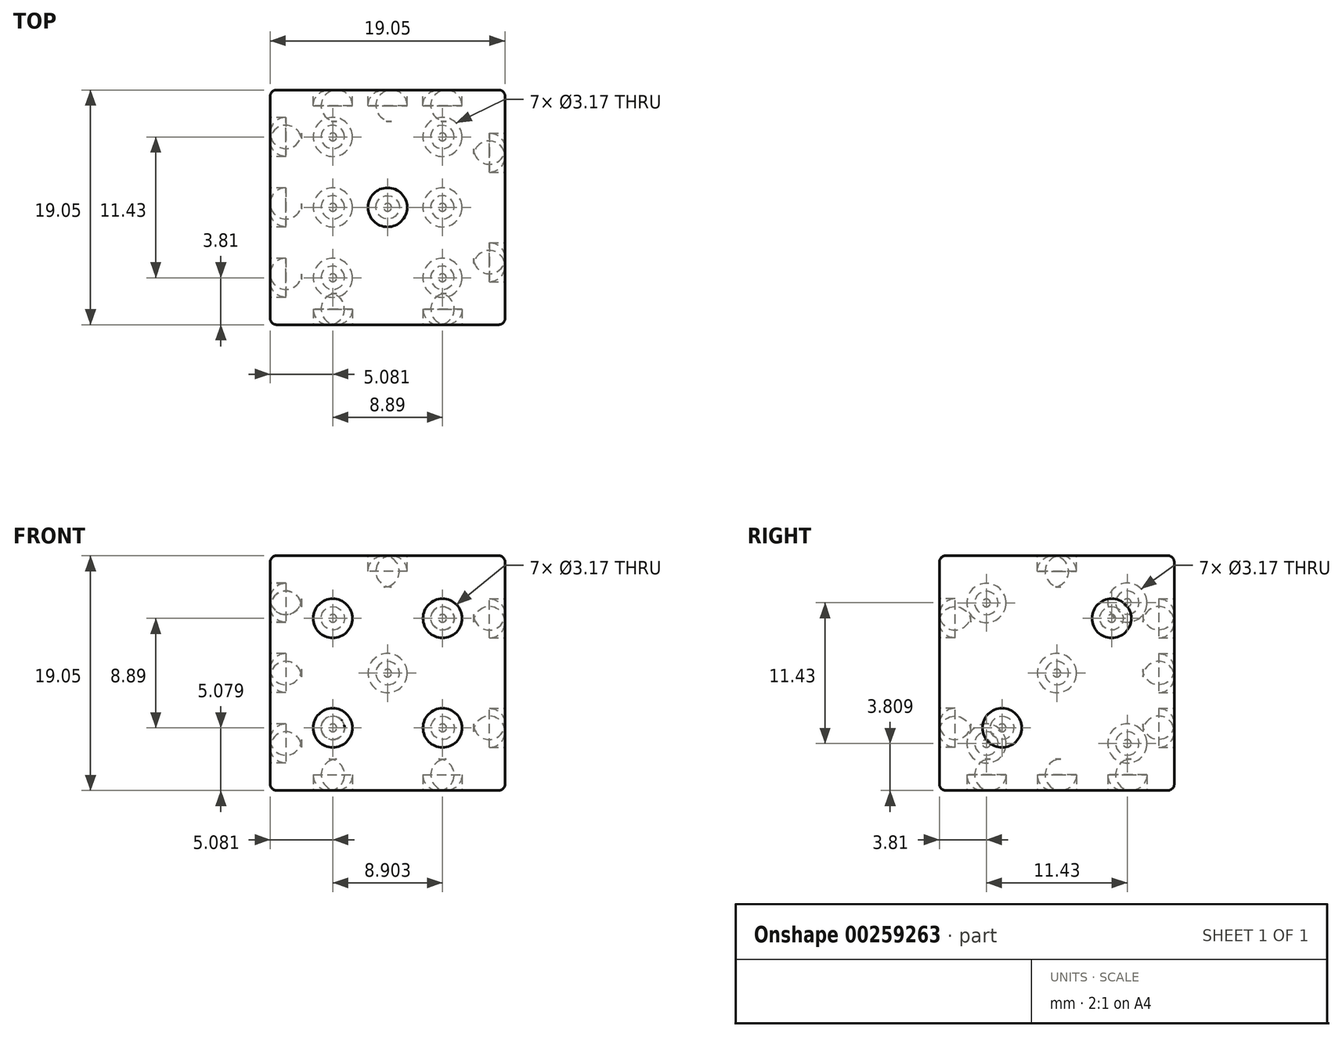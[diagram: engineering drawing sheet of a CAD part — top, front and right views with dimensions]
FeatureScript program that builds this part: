
annotation { "Feature Type Name" : "Feature", "Feature Type Description" : "" }
export const myFeature = defineFeature(function(context is Context, id is Id, definition is map)
    precondition{}
    {
        {
            var Q0;
            Q0=qCreatedBy(makeId("Front.planeOp"),FACE);
            var sketch = newSketch(context, id + "F0", { "sketchPlane" : qUnion([Q0])});
            skLineSegment(sketch, "E0.bottom", {"start": v(0, 0) * mm, "end": v(19.05, 0) * mm});
            skLineSegment(sketch, "E0.top", {"start": v(0, 19.05) * mm, "end": v(19.05, 19.05) * mm});
            skLineSegment(sketch, "E0.left", {"start": v(0, 0) * mm, "end": v(0, 19.05) * mm});
            skLineSegment(sketch, "E0.right", {"start": v(19.05, 0) * mm, "end": v(19.05, 19.05) * mm});
            skSolve(sketch);
        }
        {
            var Q0;
            Q0=makeQuery(id+"F0.imprint","IMPRINT",FACE,{"disambiguationData":[TD([[makeQuery(id+"F0.imprint","IMPRINT",EDGE,{"derivedFrom":sQuery(id+"F0.wireOp",EDGE,"E0.bottom")}),1.0]])]});
            extrude(context, id + "F1", {"entities" : qUnion([Q0]), "depth" : 19.05 * mm});
        }
        {
            var Q0;
            Q0=makeQuery(id+"F1.opExtrude","SWEPT_FACE",FACE,{"disambiguationData":[OSD([sQuery(id+"F0.wireOp",EDGE,"E0.top")])]});
            var sketch = newSketch(context, id + "F2", { "sketchPlane" : qUnion([Q0])});
            skCircle(sketch, "E1", {"center": v(9.52, -9.53) * mm, "radius": 1.59 * mm});
            skPoint(sketch, "E1.centerSnap0", {"position": v(9.52, 0) * mm});
            skPoint(sketch, "E1.centerSnap1", {"position": v(0, -9.53) * mm});
            skSolve(sketch);
        }
        {
            var Q0;
            Q0=makeQuery(id+"F2.imprint","IMPRINT",FACE,{"disambiguationData":[TD([[makeQuery(id+"F2.imprint","IMPRINT",EDGE,{"derivedFrom":sQuery(id+"F2.wireOp",EDGE,"E1")}),1.0]])]});
            extrude(context, id + "F3", {"entities" : qUnion([Q0]), "operationType" : NewBodyOperationType.REMOVE, "oppositeDirection" : true, "depth" : 2.54 * mm});
        }
        {
            var Q0;
            Q0=makeQuery(id+"F1.opExtrude","SWEPT_FACE",FACE,{"disambiguationData":[OSD([sQuery(id+"F0.wireOp",EDGE,"E0.bottom")])]});
            var sketch = newSketch(context, id + "F4", { "sketchPlane" : qUnion([Q0])});
            skCircle(sketch, "E2", {"center": v(5.08, 15.24) * mm, "radius": 1.59 * mm});
            skCircle(sketch, "E3", {"center": v(5.08, 9.53) * mm, "radius": 1.59 * mm});
            skCircle(sketch, "E4", {"center": v(5.08, 3.81) * mm, "radius": 1.59 * mm});
            skPoint(sketch, "E5", {"position": v(0, 9.53) * mm});
            skCircle(sketch, "E6", {"center": v(13.97, 15.24) * mm, "radius": 1.59 * mm});
            skCircle(sketch, "E7", {"center": v(13.97, 9.53) * mm, "radius": 1.59 * mm});
            skCircle(sketch, "E8", {"center": v(13.97, 3.81) * mm, "radius": 1.59 * mm});
            skSolve(sketch);
        }
        {
            var Q0;
            Q0=makeQuery(id+"F4.imprint","IMPRINT",FACE,{"disambiguationData":[TD([[makeQuery(id+"F4.imprint","IMPRINT",EDGE,{"derivedFrom":sQuery(id+"F4.wireOp",EDGE,"E2")}),1.0]])]});
            var Q1;
            Q1=makeQuery(id+"F4.imprint","IMPRINT",FACE,{"disambiguationData":[TD([[makeQuery(id+"F4.imprint","IMPRINT",EDGE,{"derivedFrom":sQuery(id+"F4.wireOp",EDGE,"E6")}),1.0]])]});
            var Q2;
            Q2=makeQuery(id+"F4.imprint","IMPRINT",FACE,{"disambiguationData":[TD([[makeQuery(id+"F4.imprint","IMPRINT",EDGE,{"derivedFrom":sQuery(id+"F4.wireOp",EDGE,"E7")}),1.0]])]});
            var Q3;
            Q3=makeQuery(id+"F4.imprint","IMPRINT",FACE,{"disambiguationData":[TD([[makeQuery(id+"F4.imprint","IMPRINT",EDGE,{"derivedFrom":sQuery(id+"F4.wireOp",EDGE,"E3")}),1.0]])]});
            var Q4;
            Q4=makeQuery(id+"F4.imprint","IMPRINT",FACE,{"disambiguationData":[TD([[makeQuery(id+"F4.imprint","IMPRINT",EDGE,{"derivedFrom":sQuery(id+"F4.wireOp",EDGE,"E4")}),1.0]])]});
            var Q5;
            Q5=makeQuery(id+"F4.imprint","IMPRINT",FACE,{"disambiguationData":[TD([[makeQuery(id+"F4.imprint","IMPRINT",EDGE,{"derivedFrom":sQuery(id+"F4.wireOp",EDGE,"E8")}),1.0]])]});
            extrude(context, id + "F5", {"entities" : qUnion([Q0, Q1, Q2, Q3, Q4, Q5]), "operationType" : NewBodyOperationType.REMOVE, "oppositeDirection" : true, "depth" : 2.54 * mm});
        }
        {
            var Q0;
            Q0=makeQuery(id+"F1.opExtrude","CAP_FACE",FACE,{"disambiguationData":[OSD([sQuery(id+"F0.wireOp",EDGE,"E0.bottom"),sQuery(id+"F0.wireOp",EDGE,"E0.top"),sQuery(id+"F0.wireOp",EDGE,"E0.left"),sQuery(id+"F0.wireOp",EDGE,"E0.right")])],"isStart":false});
            var sketch = newSketch(context, id + "F6", { "sketchPlane" : qUnion([Q0])});
            skCircle(sketch, "E9", {"center": v(5.08, 13.97) * mm, "radius": 1.59 * mm});
            skCircle(sketch, "E10", {"center": v(5.08, 5.08) * mm, "radius": 1.59 * mm});
            skCircle(sketch, "E11", {"center": v(13.98, 13.97) * mm, "radius": 1.59 * mm});
            skCircle(sketch, "E12", {"center": v(13.98, 5.08) * mm, "radius": 1.59 * mm});
            skSolve(sketch);
        }
        {
            var Q0;
            Q0=makeQuery(id+"F6.imprint","IMPRINT",FACE,{"disambiguationData":[TD([[makeQuery(id+"F6.imprint","IMPRINT",EDGE,{"derivedFrom":sQuery(id+"F6.wireOp",EDGE,"E9")}),1.0]])]});
            var Q1;
            Q1=makeQuery(id+"F6.imprint","IMPRINT",FACE,{"disambiguationData":[TD([[makeQuery(id+"F6.imprint","IMPRINT",EDGE,{"derivedFrom":sQuery(id+"F6.wireOp",EDGE,"E11")}),1.0]])]});
            var Q2;
            Q2=makeQuery(id+"F6.imprint","IMPRINT",FACE,{"disambiguationData":[TD([[makeQuery(id+"F6.imprint","IMPRINT",EDGE,{"derivedFrom":sQuery(id+"F6.wireOp",EDGE,"E10")}),1.0]])]});
            var Q3;
            Q3=makeQuery(id+"F6.imprint","IMPRINT",FACE,{"disambiguationData":[TD([[makeQuery(id+"F6.imprint","IMPRINT",EDGE,{"derivedFrom":sQuery(id+"F6.wireOp",EDGE,"E12")}),1.0]])]});
            extrude(context, id + "F7", {"entities" : qUnion([Q0, Q1, Q2, Q3]), "operationType" : NewBodyOperationType.REMOVE, "oppositeDirection" : true, "depth" : 2.54 * mm});
        }
        {
            var Q0;
            Q0=makeQuery(id+"F1.opExtrude","CAP_FACE",FACE,{"disambiguationData":[OSD([sQuery(id+"F0.wireOp",EDGE,"E0.bottom"),sQuery(id+"F0.wireOp",EDGE,"E0.top"),sQuery(id+"F0.wireOp",EDGE,"E0.left"),sQuery(id+"F0.wireOp",EDGE,"E0.right")])],"isStart":true});
            var sketch = newSketch(context, id + "F8", { "sketchPlane" : qUnion([Q0])});
            skCircle(sketch, "E13", {"center": v(-13.97, 13.97) * mm, "radius": 1.59 * mm});
            skCircle(sketch, "E14", {"center": v(-9.52, 9.53) * mm, "radius": 1.59 * mm});
            skPoint(sketch, "E14.centerSnap0", {"position": v(-9.52, 0) * mm});
            skPoint(sketch, "E14.centerSnap1", {"position": v(-19.05, 9.53) * mm});
            skCircle(sketch, "E15", {"center": v(-5.08, 5.08) * mm, "radius": 1.59 * mm});
            skSolve(sketch);
        }
        {
            var Q0;
            Q0=makeQuery(id+"F8.imprint","IMPRINT",FACE,{"disambiguationData":[TD([[makeQuery(id+"F8.imprint","IMPRINT",EDGE,{"derivedFrom":sQuery(id+"F8.wireOp",EDGE,"E13")}),1.0]])]});
            var Q1;
            Q1=makeQuery(id+"F8.imprint","IMPRINT",FACE,{"disambiguationData":[TD([[makeQuery(id+"F8.imprint","IMPRINT",EDGE,{"derivedFrom":sQuery(id+"F8.wireOp",EDGE,"E14")}),1.0]])]});
            var Q2;
            Q2=makeQuery(id+"F8.imprint","IMPRINT",FACE,{"disambiguationData":[TD([[makeQuery(id+"F8.imprint","IMPRINT",EDGE,{"derivedFrom":sQuery(id+"F8.wireOp",EDGE,"E15")}),1.0]])]});
            extrude(context, id + "F9", {"entities" : qUnion([Q0, Q1, Q2]), "operationType" : NewBodyOperationType.REMOVE, "oppositeDirection" : true, "depth" : 2.54 * mm});
        }
        {
            var Q0;
            Q0=makeQuery(id+"F1.opExtrude","SWEPT_FACE",FACE,{"disambiguationData":[OSD([sQuery(id+"F0.wireOp",EDGE,"E0.left")])]});
            var sketch = newSketch(context, id + "F10", { "sketchPlane" : qUnion([Q0])});
            skCircle(sketch, "E16", {"center": v(3.81, 15.24) * mm, "radius": 1.59 * mm});
            skCircle(sketch, "E17", {"center": v(9.53, 9.53) * mm, "radius": 1.59 * mm});
            skPoint(sketch, "E17.centerSnap0", {"position": v(9.53, 19.05) * mm});
            skPoint(sketch, "E17.centerSnap1", {"position": v(0, 9.53) * mm});
            skCircle(sketch, "E18", {"center": v(15.24, 15.22) * mm, "radius": 1.59 * mm});
            skCircle(sketch, "E19", {"center": v(3.81, 3.81) * mm, "radius": 1.59 * mm});
            skCircle(sketch, "E20", {"center": v(15.24, 3.81) * mm, "radius": 1.59 * mm});
            skSolve(sketch);
        }
        {
            var Q0;
            Q0 = qSketchRegion(id + "F10", true);
            extrude(context, id + "F11", {"entities" : qUnion([Q0]), "operationType" : NewBodyOperationType.REMOVE, "oppositeDirection" : true, "depth" : 2.54 * mm});
        }
        {
            var Q0;
            Q0=makeQuery(id+"F1.opExtrude","SWEPT_FACE",FACE,{"disambiguationData":[OSD([sQuery(id+"F0.wireOp",EDGE,"E0.right")])]});
            var sketch = newSketch(context, id + "F12", { "sketchPlane" : qUnion([Q0])});
            skCircle(sketch, "E21", {"center": v(-5.08, 13.97) * mm, "radius": 1.59 * mm});
            skCircle(sketch, "E22", {"center": v(-13.97, 5.08) * mm, "radius": 1.59 * mm});
            skSolve(sketch);
        }
        {
            var Q0;
            Q0 = qSketchRegion(id + "F12", true);
            extrude(context, id + "F13", {"entities" : qUnion([Q0]), "operationType" : NewBodyOperationType.REMOVE, "oppositeDirection" : true, "depth" : 2.54 * mm});
        }
        {
            var Q0;
            Q0=makeQuery(id+"F13.boolean.opBoolean","COPY",EDGE,{"derivedFrom":makeQuery(id+"F13.opExtrude","CAP_EDGE",EDGE,{"disambiguationData":[OSD([sQuery(id+"F12.wireOp",EDGE,"E22")])],"isStart":false})});
            fillet(context, id + "F14", {"entities" : qUnion([Q0]), "radius" : 1.27 * mm, "tangentPropagation" : true, "allowEdgeOverflow" : false});
        }
        {
            var Q0;
            Q0=makeQuery(id+"F13.boolean.opBoolean","COPY",EDGE,{"derivedFrom":makeQuery(id+"F13.opExtrude","CAP_EDGE",EDGE,{"disambiguationData":[OSD([sQuery(id+"F12.wireOp",EDGE,"E21")])],"isStart":false})});
            fillet(context, id + "F15", {"entities" : qUnion([Q0]), "radius" : 1.27 * mm, "tangentPropagation" : true, "allowEdgeOverflow" : false});
        }
        {
            var Q0;
            Q0=makeQuery(id+"F3.boolean.opBoolean","COPY",EDGE,{"derivedFrom":makeQuery(id+"F3.opExtrude","CAP_EDGE",EDGE,{"disambiguationData":[OSD([sQuery(id+"F2.wireOp",EDGE,"E1")])],"isStart":false})});
            fillet(context, id + "F16", {"entities" : qUnion([Q0]), "radius" : 1.27 * mm, "tangentPropagation" : true, "allowEdgeOverflow" : false});
        }
        {
            var Q0;
            Q0=makeQuery(id+"F11.boolean.opBoolean","COPY",EDGE,{"derivedFrom":makeQuery(id+"F11.opExtrude","CAP_EDGE",EDGE,{"disambiguationData":[OSD([sQuery(id+"F10.wireOp",EDGE,"E18")])],"isStart":false})});
            var Q1;
            Q1=makeQuery(id+"F11.boolean.opBoolean","COPY",EDGE,{"derivedFrom":makeQuery(id+"F11.opExtrude","CAP_EDGE",EDGE,{"disambiguationData":[OSD([sQuery(id+"F10.wireOp",EDGE,"E20")])],"isStart":false})});
            var Q2;
            Q2=makeQuery(id+"F11.boolean.opBoolean","COPY",EDGE,{"derivedFrom":makeQuery(id+"F11.opExtrude","CAP_EDGE",EDGE,{"disambiguationData":[OSD([sQuery(id+"F10.wireOp",EDGE,"E17")])],"isStart":false})});
            var Q3;
            Q3=makeQuery(id+"F11.boolean.opBoolean","COPY",EDGE,{"derivedFrom":makeQuery(id+"F11.opExtrude","CAP_EDGE",EDGE,{"disambiguationData":[OSD([sQuery(id+"F10.wireOp",EDGE,"E19")])],"isStart":false})});
            var Q4;
            Q4=makeQuery(id+"F11.boolean.opBoolean","COPY",EDGE,{"derivedFrom":makeQuery(id+"F11.opExtrude","CAP_EDGE",EDGE,{"disambiguationData":[OSD([sQuery(id+"F10.wireOp",EDGE,"E16")])],"isStart":false})});
            fillet(context, id + "F17", {"entities" : qUnion([Q0, Q1, Q2, Q3, Q4]), "radius" : 1.27 * mm, "tangentPropagation" : true, "allowEdgeOverflow" : false});
        }
        {
            var Q0;
            Q0=makeQuery(id+"F9.boolean.opBoolean","COPY",EDGE,{"derivedFrom":makeQuery(id+"F9.opExtrude","CAP_EDGE",EDGE,{"disambiguationData":[OSD([sQuery(id+"F8.wireOp",EDGE,"E15")])],"isStart":false})});
            var Q1;
            Q1=makeQuery(id+"F9.boolean.opBoolean","COPY",EDGE,{"derivedFrom":makeQuery(id+"F9.opExtrude","CAP_EDGE",EDGE,{"disambiguationData":[OSD([sQuery(id+"F8.wireOp",EDGE,"E14")])],"isStart":false})});
            var Q2;
            Q2=makeQuery(id+"F9.boolean.opBoolean","COPY",EDGE,{"derivedFrom":makeQuery(id+"F9.opExtrude","CAP_EDGE",EDGE,{"disambiguationData":[OSD([sQuery(id+"F8.wireOp",EDGE,"E13")])],"isStart":false})});
            fillet(context, id + "F18", {"entities" : qUnion([Q0, Q1, Q2]), "radius" : 1.27 * mm, "tangentPropagation" : true, "allowEdgeOverflow" : false});
        }
        {
            var Q0;
            Q0=makeQuery(id+"F5.boolean.opBoolean","COPY",EDGE,{"derivedFrom":makeQuery(id+"F5.opExtrude","CAP_EDGE",EDGE,{"disambiguationData":[OSD([sQuery(id+"F4.wireOp",EDGE,"E4")])],"isStart":false})});
            var Q1;
            Q1=makeQuery(id+"F5.boolean.opBoolean","COPY",EDGE,{"derivedFrom":makeQuery(id+"F5.opExtrude","CAP_EDGE",EDGE,{"disambiguationData":[OSD([sQuery(id+"F4.wireOp",EDGE,"E3")])],"isStart":false})});
            var Q2;
            Q2=makeQuery(id+"F5.boolean.opBoolean","COPY",EDGE,{"derivedFrom":makeQuery(id+"F5.opExtrude","CAP_EDGE",EDGE,{"disambiguationData":[OSD([sQuery(id+"F4.wireOp",EDGE,"E2")])],"isStart":false})});
            var Q3;
            Q3=makeQuery(id+"F5.boolean.opBoolean","COPY",EDGE,{"derivedFrom":makeQuery(id+"F5.opExtrude","CAP_EDGE",EDGE,{"disambiguationData":[OSD([sQuery(id+"F4.wireOp",EDGE,"E6")])],"isStart":false})});
            var Q4;
            Q4=makeQuery(id+"F5.boolean.opBoolean","COPY",EDGE,{"derivedFrom":makeQuery(id+"F5.opExtrude","CAP_EDGE",EDGE,{"disambiguationData":[OSD([sQuery(id+"F4.wireOp",EDGE,"E7")])],"isStart":false})});
            var Q5;
            Q5=makeQuery(id+"F5.boolean.opBoolean","COPY",EDGE,{"derivedFrom":makeQuery(id+"F5.opExtrude","CAP_EDGE",EDGE,{"disambiguationData":[OSD([sQuery(id+"F4.wireOp",EDGE,"E8")])],"isStart":false})});
            fillet(context, id + "F19", {"entities" : qUnion([Q0, Q1, Q2, Q3, Q4, Q5]), "radius" : 1.27 * mm, "tangentPropagation" : true, "allowEdgeOverflow" : false});
        }
        {
            var Q0;
            Q0=makeQuery(id+"F7.boolean.opBoolean","COPY",EDGE,{"derivedFrom":makeQuery(id+"F7.opExtrude","CAP_EDGE",EDGE,{"disambiguationData":[OSD([sQuery(id+"F6.wireOp",EDGE,"E10")])],"isStart":false})});
            var Q1;
            Q1=makeQuery(id+"F7.boolean.opBoolean","COPY",EDGE,{"derivedFrom":makeQuery(id+"F7.opExtrude","CAP_EDGE",EDGE,{"disambiguationData":[OSD([sQuery(id+"F6.wireOp",EDGE,"E9")])],"isStart":false})});
            var Q2;
            Q2=makeQuery(id+"F7.boolean.opBoolean","COPY",EDGE,{"derivedFrom":makeQuery(id+"F7.opExtrude","CAP_EDGE",EDGE,{"disambiguationData":[OSD([sQuery(id+"F6.wireOp",EDGE,"E11")])],"isStart":false})});
            var Q3;
            Q3=makeQuery(id+"F7.boolean.opBoolean","COPY",EDGE,{"derivedFrom":makeQuery(id+"F7.opExtrude","CAP_EDGE",EDGE,{"disambiguationData":[OSD([sQuery(id+"F6.wireOp",EDGE,"E12")])],"isStart":false})});
            fillet(context, id + "F20", {"entities" : qUnion([Q0, Q1, Q2, Q3]), "radius" : 1.27 * mm, "tangentPropagation" : true, "allowEdgeOverflow" : false});
        }
        {
            var Q0;
            Q0=makeQuery(id+"F1.opExtrude","SWEPT_BODY",BODY,{"disambiguationData":[OSD([sQuery(id+"F0.wireOp",EDGE,"E0.bottom"),sQuery(id+"F0.wireOp",EDGE,"E0.top"),sQuery(id+"F0.wireOp",EDGE,"E0.left"),sQuery(id+"F0.wireOp",EDGE,"E0.right")])]});
            var Q1;
            Q1=makeQuery(id+"F1.opExtrude","SWEPT_EDGE",EDGE,{"disambiguationData":[OSD([sQuery(id+"F0.wireOp",EDGE,"E0.bottom"),sQuery(id+"F0.wireOp",EDGE,"E0.left")])]});
            transform(context, id + "F21", {"entities" : qUnion([Q0]), "transformType" : TransformType.ROTATION, "transformAxis" : qUnion([Q1]), "angle" : 45 * degree, "oppositeDirection" : true, "makeCopy" : false});
        }
        {
            var Q0;
            Q0=makeQuery(id+"F1.opExtrude","CAP_EDGE",EDGE,{"disambiguationData":[OSD([sQuery(id+"F0.wireOp",EDGE,"E0.top")])],"isStart":false});
            var Q1;
            Q1=makeQuery(id+"F1.opExtrude","CAP_EDGE",EDGE,{"disambiguationData":[OSD([sQuery(id+"F0.wireOp",EDGE,"E0.right")])],"isStart":false});
            var Q2;
            Q2=makeQuery(id+"F1.opExtrude","CAP_EDGE",EDGE,{"disambiguationData":[OSD([sQuery(id+"F0.wireOp",EDGE,"E0.bottom")])],"isStart":false});
            var Q3;
            Q3=makeQuery(id+"F1.opExtrude","CAP_EDGE",EDGE,{"disambiguationData":[OSD([sQuery(id+"F0.wireOp",EDGE,"E0.left")])],"isStart":false});
            var Q4;
            Q4=makeQuery(id+"F1.opExtrude","SWEPT_EDGE",EDGE,{"disambiguationData":[OSD([sQuery(id+"F0.wireOp",EDGE,"E0.bottom"),sQuery(id+"F0.wireOp",EDGE,"E0.left")])]});
            var Q5;
            Q5=makeQuery(id+"F1.opExtrude","CAP_EDGE",EDGE,{"disambiguationData":[OSD([sQuery(id+"F0.wireOp",EDGE,"E0.left")])],"isStart":true});
            var Q6;
            Q6=makeQuery(id+"F1.opExtrude","SWEPT_EDGE",EDGE,{"disambiguationData":[OSD([sQuery(id+"F0.wireOp",EDGE,"E0.top"),sQuery(id+"F0.wireOp",EDGE,"E0.left")])]});
            var Q7;
            Q7=makeQuery(id+"F1.opExtrude","CAP_EDGE",EDGE,{"disambiguationData":[OSD([sQuery(id+"F0.wireOp",EDGE,"E0.bottom")])],"isStart":true});
            var Q8;
            Q8=makeQuery(id+"F1.opExtrude","CAP_EDGE",EDGE,{"disambiguationData":[OSD([sQuery(id+"F0.wireOp",EDGE,"E0.right")])],"isStart":true});
            var Q9;
            Q9=makeQuery(id+"F1.opExtrude","CAP_EDGE",EDGE,{"disambiguationData":[OSD([sQuery(id+"F0.wireOp",EDGE,"E0.top")])],"isStart":true});
            var Q10;
            Q10=makeQuery(id+"F1.opExtrude","SWEPT_EDGE",EDGE,{"disambiguationData":[OSD([sQuery(id+"F0.wireOp",EDGE,"E0.top"),sQuery(id+"F0.wireOp",EDGE,"E0.right")])]});
            var Q11;
            Q11=makeQuery(id+"F1.opExtrude","SWEPT_EDGE",EDGE,{"disambiguationData":[OSD([sQuery(id+"F0.wireOp",EDGE,"E0.bottom"),sQuery(id+"F0.wireOp",EDGE,"E0.right")])]});
            fillet(context, id + "F22", {"entities" : qUnion([Q0, Q1, Q2, Q3, Q4, Q5, Q6, Q7, Q8, Q9, Q10, Q11]), "radius" : 0.5 * mm, "tangentPropagation" : true, "allowEdgeOverflow" : false});
        }
        {
            var Q0;
            Q0=makeQuery(id+"F1.opExtrude","SWEPT_BODY",BODY,{"disambiguationData":[OSD([sQuery(id+"F0.wireOp",EDGE,"E0.bottom"),sQuery(id+"F0.wireOp",EDGE,"E0.top"),sQuery(id+"F0.wireOp",EDGE,"E0.left"),sQuery(id+"F0.wireOp",EDGE,"E0.right")])]});
            var Q1;
            {var subQ0=sQuery(id+"F0.wireOp",EDGE,"E0.bottom");Q1=makeQuery(id+"F22.opFillet","BLEND_EDGE",EDGE,{"blendedFrom":[makeQuery(id+"F1.opExtrude","SWEPT_EDGE",EDGE,{"disambiguationData":[OSD([subQ0,sQuery(id+"F0.wireOp",EDGE,"E0.left")])]}),makeQuery(id+"F1.opExtrude","SWEPT_FACE",FACE,{"disambiguationData":[OSD([subQ0])]})],"blendedInto":[makeQuery(id+"F1.opExtrude","SWEPT_FACE",FACE,{"disambiguationData":[OSD([subQ0])]})]});}
            transform(context, id + "F23", {"entities" : qUnion([Q0]), "transformType" : TransformType.ROTATION, "transformAxis" : qUnion([Q1]), "angle" : 45 * degree, "makeCopy" : false});
        }
    });
